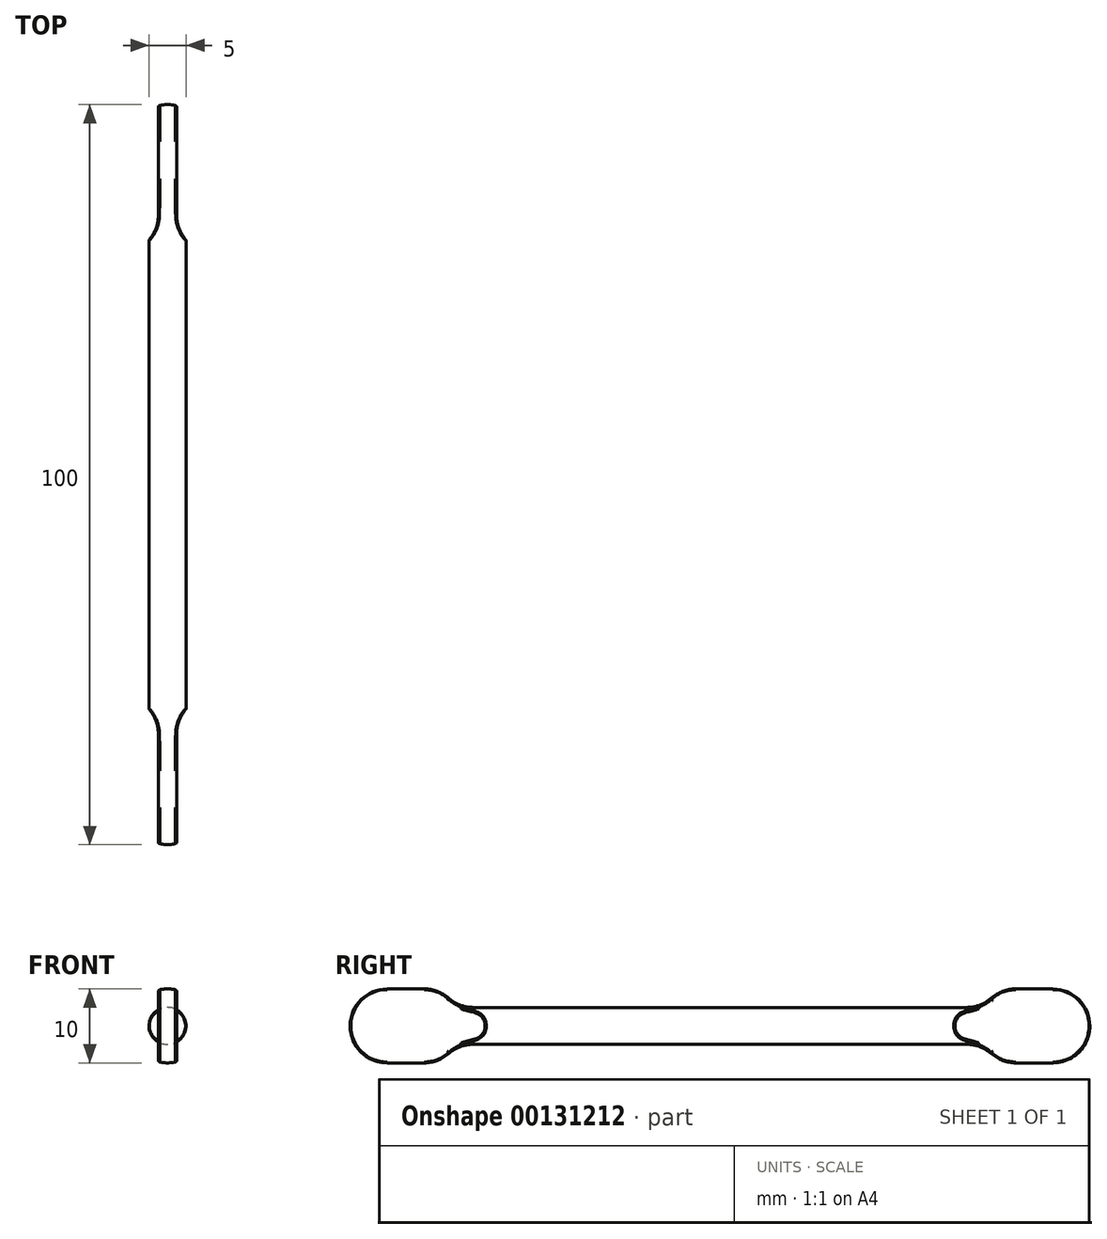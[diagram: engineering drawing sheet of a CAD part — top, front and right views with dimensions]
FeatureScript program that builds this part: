
annotation { "Feature Type Name" : "Feature", "Feature Type Description" : "" }
export const myFeature = defineFeature(function(context is Context, id is Id, definition is map)
    precondition{}
    {
        {
            var Q0;
            Q0=qCreatedBy(makeId("Right.planeOp"),FACE);
            var sketch = newSketch(context, id + "F0", { "sketchPlane" : qUnion([Q0])});
            skLineSegment(sketch, "E0", {"start": v(0, 2.5) * mm, "end": v(35.67, 2.5) * mm});
            skLineSegment(sketch, "E1", {"start": v(50, 0) * mm, "end": v(0, 0) * mm});
            skLineSegment(sketch, "E2", {"start": v(0, 0) * mm, "end": v(0, 2.5) * mm});
            skLineSegment(sketch, "E3", {"start": v(40, 5) * mm, "end": v(45, 5) * mm});
            skArc(sketch, "E4", {"start": v(40, 5) * mm, "mid": v(37.5, 4.33) * mm, "end": v(35.67, 2.5) * mm});
            skArc(sketch, "E5", {"start": v(50, 0) * mm, "mid": v(48.54, 3.54) * mm, "end": v(45, 5) * mm});
            skSolve(sketch);
        }
        {
            var Q0;
            Q0 = qSketchRegion(id + "F0", true);
            var Q1;
            Q1=sQuery(id+"F0.wireOp",EDGE,"E1");
            revolve(context, id + "F1", {"entities" : qUnion([Q0]), "axis" : qUnion([Q1]), "revolveType" : RevolveType.FULL});
        }
        {
            var Q0;
            Q0=makeQuery(id+"F1.opRevolve","SWEPT_EDGE",EDGE,{"disambiguationData":[OSD([sQuery(id+"F0.wireOp",EDGE,"E0"),sQuery(id+"F0.wireOp",EDGE,"E4")])]});
            fillet(context, id + "F2", {"entities" : qUnion([Q0]), "radius" : 5 * mm, "tangentPropagation" : true, "allowEdgeOverflow" : false});
        }
        {
            var Q0;
            Q0=qCreatedBy(makeId("Top.planeOp"),FACE);
            var sketch = newSketch(context, id + "F3", { "sketchPlane" : qUnion([Q0])});
            skLineSegment(sketch, "E6.bottom", {"start": v(-25, 30) * mm, "end": v(-6.25, 30) * mm});
            skLineSegment(sketch, "E6.top", {"start": v(-25, 75) * mm, "end": v(-1.25, 75) * mm});
            skLineSegment(sketch, "E6.left", {"start": v(-25, 30) * mm, "end": v(-25, 75) * mm});
            skLineSegment(sketch, "E6.right", {"start": v(-1.25, 35) * mm, "end": v(-1.25, 75) * mm});
            skPoint(sketch, "E7.visualSharp", {"position": v(-1.25, 30) * mm});
            skArc(sketch, "E7.filletArc", {"start": v(-6.25, 30) * mm, "mid": v(-2.71, 31.46) * mm, "end": v(-1.25, 35) * mm});
            skSolve(sketch);
        }
        {
            var Q0;
            Q0 = qSketchRegion(id + "F3", true);
            extrude(context, id + "F4", {"entities" : qUnion([Q0]), "endBound" : BoundingType.THROUGH_ALL, "oppositeDirection" : true, "depth" : 25 * mm, "hasSecondDirection" : true, "secondDirectionBound" : BoundingType.THROUGH_ALL, "secondDirectionOppositeDirection" : false, "secondDirectionDepth" : 25 * mm});
        }
        {
            var Q0;
            Q0=makeQuery(id+"F4.opExtrude","SWEPT_BODY",BODY,{"disambiguationData":[OSD([sQuery(id+"F3.wireOp",EDGE,"E6.bottom"),sQuery(id+"F3.wireOp",EDGE,"E6.top"),sQuery(id+"F3.wireOp",EDGE,"E6.left"),sQuery(id+"F3.wireOp",EDGE,"E6.right"),sQuery(id+"F3.wireOp",EDGE,"E7.filletArc")])]});
            var Q1;
            Q1=qCreatedBy(makeId("Right.planeOp"),FACE);
            mirror(context, id + "F5", {"entities" : qUnion([Q0]), "mirrorPlane" : qUnion([Q1])});
        }
        {
            var Q0;
            Q0=makeQuery(id+"F4.opExtrude","SWEPT_BODY",BODY,{"disambiguationData":[OSD([sQuery(id+"F3.wireOp",EDGE,"E6.bottom"),sQuery(id+"F3.wireOp",EDGE,"E6.top"),sQuery(id+"F3.wireOp",EDGE,"E6.left"),sQuery(id+"F3.wireOp",EDGE,"E6.right"),sQuery(id+"F3.wireOp",EDGE,"E7.filletArc")])]});
            var Q1;
            Q1=makeQuery(id+"F5.opPattern","COPY",BODY,{"derivedFrom":makeQuery(id+"F4.opExtrude","SWEPT_BODY",BODY,{"disambiguationData":[OSD([sQuery(id+"F3.wireOp",EDGE,"E6.bottom"),sQuery(id+"F3.wireOp",EDGE,"E6.top"),sQuery(id+"F3.wireOp",EDGE,"E6.left"),sQuery(id+"F3.wireOp",EDGE,"E6.right"),sQuery(id+"F3.wireOp",EDGE,"E7.filletArc")])]}),"instanceName":"1"});
            var Q2;
            Q2=makeQuery(id+"F1.opRevolve","SWEPT_BODY",BODY,{"disambiguationData":[OSD([sQuery(id+"F0.wireOp",EDGE,"E0"),sQuery(id+"F0.wireOp",EDGE,"E1"),sQuery(id+"F0.wireOp",EDGE,"E2"),sQuery(id+"F0.wireOp",EDGE,"E3"),sQuery(id+"F0.wireOp",EDGE,"E4"),sQuery(id+"F0.wireOp",EDGE,"E5")])]});
            booleanBodies(context, id + "F6", {"operationType" : BooleanOperationType.SUBTRACTION, "tools" : qUnion([Q0, Q1]), "targets" : qUnion([Q2])});
        }
        {
            var Q0;
            Q0=makeQuery(id+"F6.opBoolean","INTERSECT",EDGE,{"derivedFrom":[makeQuery(id+"F1.opRevolve","SWEPT_FACE",FACE,{"disambiguationData":[OSD([sQuery(id+"F0.wireOp",EDGE,"E5")])]}),makeQuery(id+"F4.opExtrude","SWEPT_FACE",FACE,{"disambiguationData":[OSD([sQuery(id+"F3.wireOp",EDGE,"E6.right")])]})]});
            var Q1;
            Q1=makeQuery(id+"F6.opBoolean","INTERSECT",EDGE,{"derivedFrom":[makeQuery(id+"F1.opRevolve","SWEPT_FACE",FACE,{"disambiguationData":[OSD([sQuery(id+"F0.wireOp",EDGE,"E5")])]}),makeQuery(id+"F5.opPattern","COPY",FACE,{"derivedFrom":makeQuery(id+"F4.opExtrude","SWEPT_FACE",FACE,{"disambiguationData":[OSD([sQuery(id+"F3.wireOp",EDGE,"E6.right")])]}),"instanceName":"1"})]});
            fillet(context, id + "F7", {"entities" : qUnion([Q0, Q1]), "radius" : .25 * mm, "tangentPropagation" : true, "allowEdgeOverflow" : false});
        }
        {
            var Q0;
            Q0=makeQuery(id+"F1.opRevolve","SWEPT_BODY",BODY,{"disambiguationData":[OSD([sQuery(id+"F0.wireOp",EDGE,"E0"),sQuery(id+"F0.wireOp",EDGE,"E1"),sQuery(id+"F0.wireOp",EDGE,"E2"),sQuery(id+"F0.wireOp",EDGE,"E3"),sQuery(id+"F0.wireOp",EDGE,"E4"),sQuery(id+"F0.wireOp",EDGE,"E5")])]});
            var Q1;
            Q1=qCreatedBy(makeId("Front.planeOp"),FACE);
            mirror(context, id + "F8", {"operationType" : NewBodyOperationType.ADD, "entities" : qUnion([Q0]), "mirrorPlane" : qUnion([Q1])});
        }
    });
